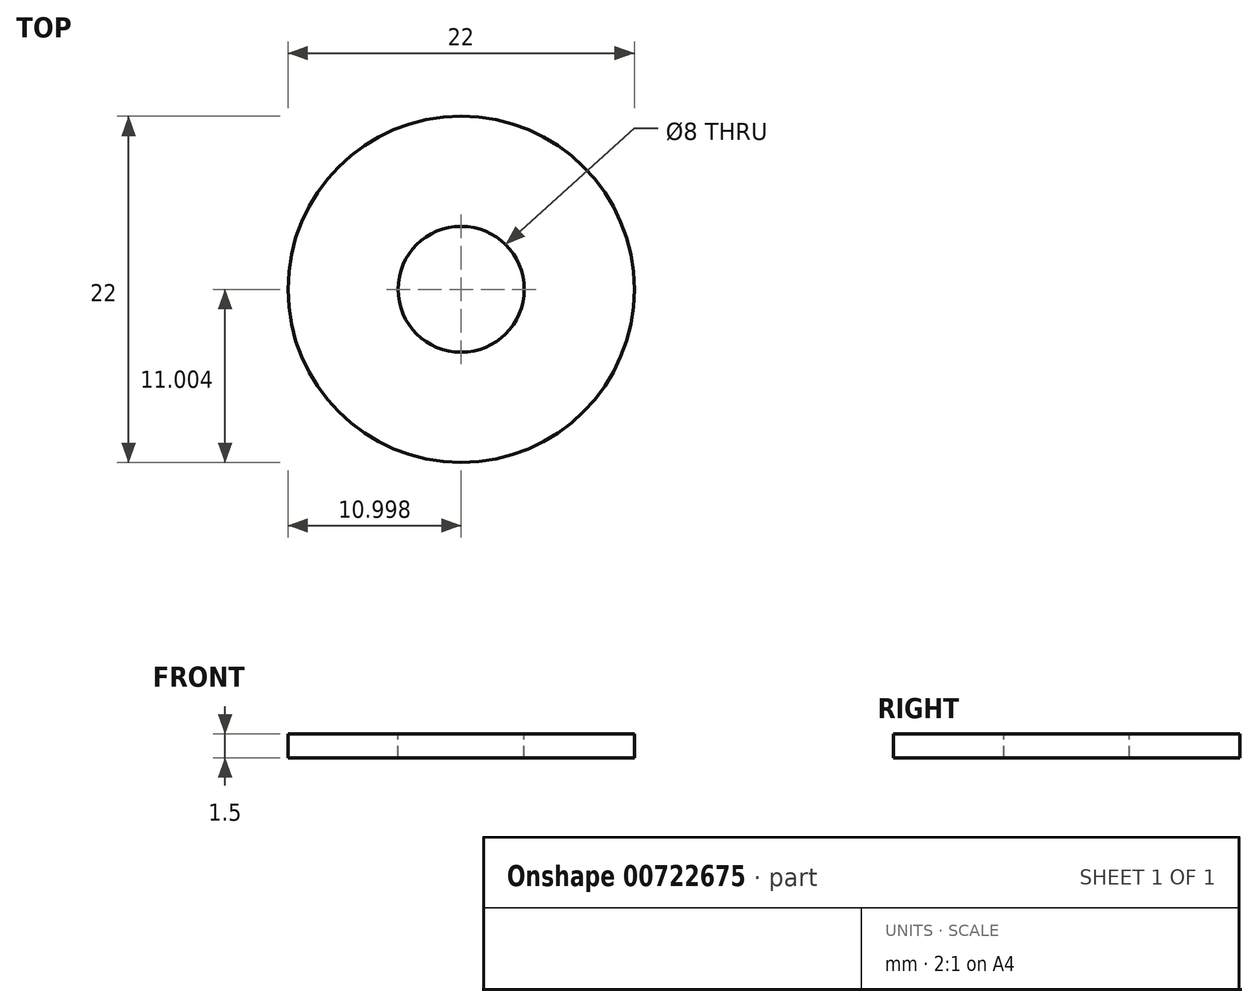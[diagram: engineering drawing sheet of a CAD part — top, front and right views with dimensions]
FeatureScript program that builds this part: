
annotation { "Feature Type Name" : "Feature", "Feature Type Description" : "" }
export const myFeature = defineFeature(function(context is Context, id is Id, definition is map)
    precondition{}
    {
        {
            var Q0;
            Q0=qCreatedBy(makeId("Top.planeOp"),FACE);
            var sketch = newSketch(context, id + "F0", { "sketchPlane" : qUnion([Q0])});
            skCircle(sketch, "E0", {"center": v(-33.32, 31.8) * mm, "radius": 11 * mm});
            skSolve(sketch);
        }
        {
            var Q0;
            Q0=makeQuery(id+"F0.imprint","IMPRINT",FACE,{"disambiguationData":[TD([[makeQuery(id+"F0.imprint","IMPRINT",EDGE,{"derivedFrom":sQuery(id+"F0.wireOp",EDGE,"E0")}),1.0]])]});
            extrude(context, id + "F1", {"entities" : qUnion([Q0]), "depth" : 1.5 * mm, "offsetDistance" : 25 * mm});
        }
        {
            var Q0;
            Q0=makeQuery(id+"F1.opExtrude","CAP_FACE",FACE,{"disambiguationData":[OSD([sQuery(id+"F0.wireOp",EDGE,"E0")])],"isStart":false});
            var sketch = newSketch(context, id + "F2", { "sketchPlane" : qUnion([Q0])});
            skCircle(sketch, "E1", {"center": v(-33.32, 31.8) * mm, "radius": 4 * mm});
            skSolve(sketch);
        }
        {
            var Q0;
            Q0=makeQuery(id+"F2.imprint","IMPRINT",FACE,{"disambiguationData":[TD([[makeQuery(id+"F2.imprint","IMPRINT",EDGE,{"derivedFrom":sQuery(id+"F2.wireOp",EDGE,"E1")}),1.0]])]});
            extrude(context, id + "F3", {"entities" : qUnion([Q0]), "operationType" : NewBodyOperationType.REMOVE, "oppositeDirection" : true, "depth" : 25 * mm, "offsetDistance" : 25 * mm});
        }
        {
            var Q0;
            Q0=makeQuery(id+"F1.opExtrude","SWEPT_BODY",BODY,{"disambiguationData":[OSD([sQuery(id+"F0.wireOp",EDGE,"E0")])]});
            transform(context, id + "F4", {"entities" : qUnion([Q0]), "transformType" : TransformType.TRANSLATION_3D, "dx" : 22.4 * mm, "dy" : -20.8 * mm, "dz" : 0 * mm, "makeCopy" : false});
        }
    });
